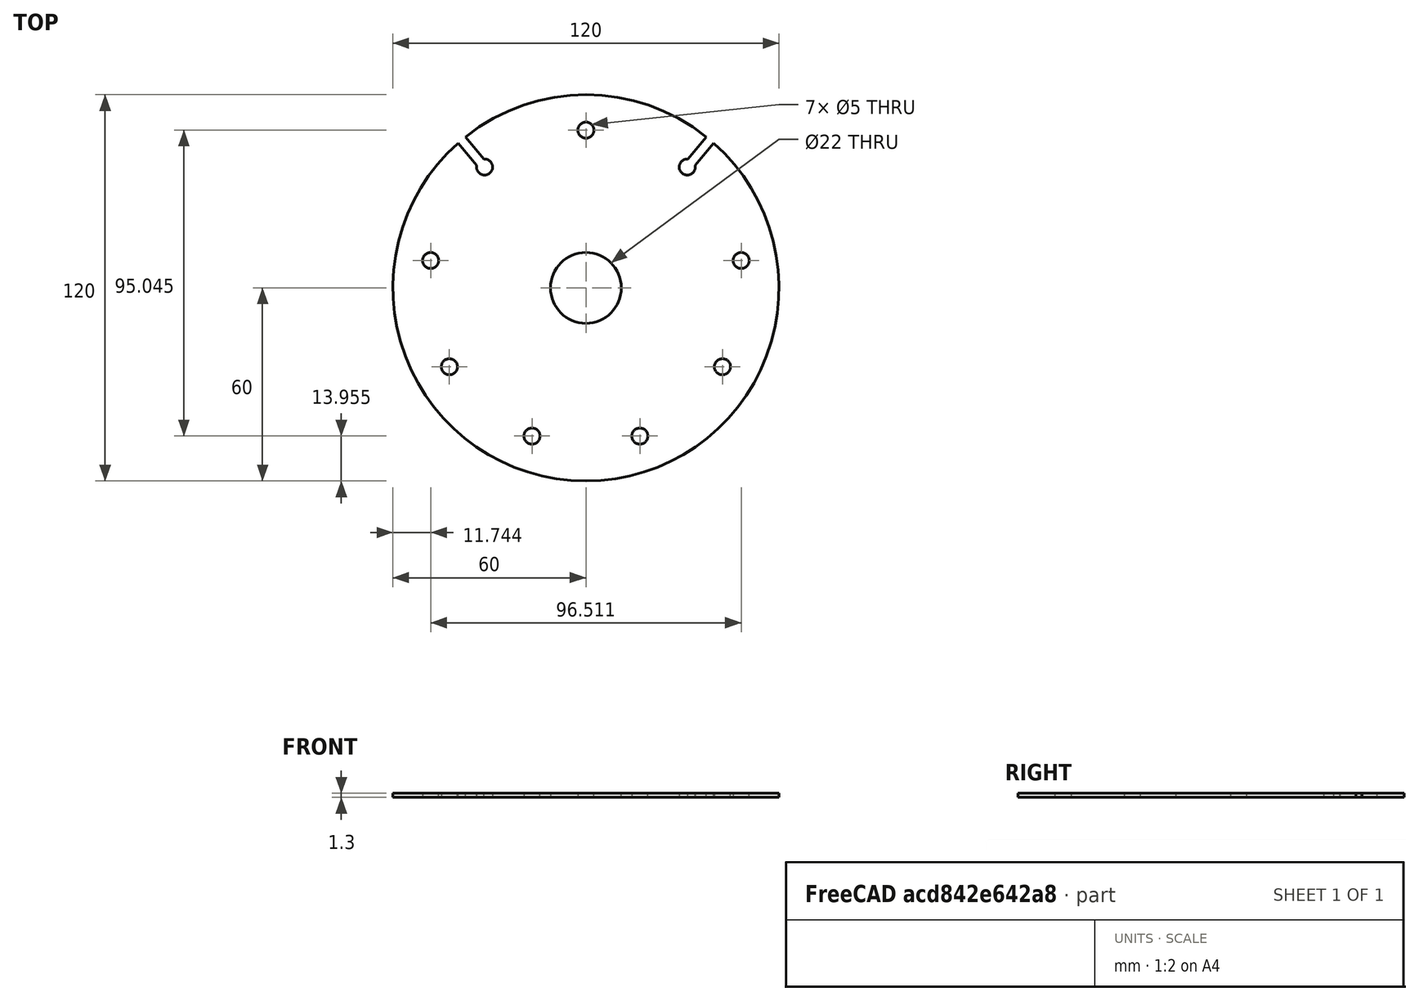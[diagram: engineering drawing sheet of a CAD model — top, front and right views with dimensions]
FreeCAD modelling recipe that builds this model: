
FCSTD DOCUMENT  (FreeCAD 0.19R24276 (Git))
Label: Disk_bolgarki_v2_d22_d120
License: All rights reserved
LicenseURL: http://en.wikipedia.org/wiki/All_rights_reserved
objects: Sketcher::SketchObject×1, PartDesign::Pad×1, PartDesign::Body×1
note: 4 computed .brp shape members not serialized (recipe doc carries the construction recipe); baked Part::Feature solids carry a one-line shape summary decoded from their .brp

FEATURE [Sketcher::SketchObject] Sketch
  FullyConstrained = false
  MapMode = 5
  Support = -> [XY_Plane]
  sketch-geometry (35):
    g0: Circle CenterX=0 CenterY=0 CenterZ=0 NormalX=0 NormalY=0 NormalZ=1 AngleXU=0 Radius=11
    g1: ArcOfCircle CenterX=0 CenterY=0 CenterZ=0 NormalX=0 NormalY=0 NormalZ=1 AngleXU=0 Radius=60 StartAngle=0.897667 EndAngle=2.24393
    g2: LineSegment StartX=0 StartY=49 StartZ=0 EndX=-31.4966 EndY=37.5362 EndZ=0
    g3: LineSegment StartX=-31.4966 StartY=37.5362 StartZ=0 EndX=-48.2556 EndY=8.50876 EndZ=0
    g4: LineSegment StartX=-48.2556 StartY=8.50876 StartZ=0 EndX=-42.4352 EndY=-24.5 EndZ=0
    g5: LineSegment StartX=-42.4352 StartY=-24.5 StartZ=0 EndX=-16.759 EndY=-46.0449 EndZ=0
    g6: LineSegment StartX=-16.759 StartY=-46.0449 StartZ=0 EndX=16.759 EndY=-46.0449 EndZ=0
    g7: LineSegment StartX=16.759 StartY=-46.0449 StartZ=0 EndX=42.4352 EndY=-24.5 EndZ=0
    g8: LineSegment StartX=42.4352 StartY=-24.5 StartZ=0 EndX=48.2556 EndY=8.50876 EndZ=0
    g9: LineSegment StartX=48.2556 StartY=8.50876 StartZ=0 EndX=31.4966 EndY=37.5362 EndZ=0
    g10: LineSegment StartX=31.4966 StartY=37.5362 StartZ=0 EndX=0 EndY=49 EndZ=0
    g11: Circle CenterX=0 CenterY=0 CenterZ=0 NormalX=0 NormalY=0 NormalZ=1 AngleXU=0 Radius=49
    g12: Circle CenterX=0 CenterY=49 CenterZ=0 NormalX=0 NormalY=0 NormalZ=1 AngleXU=0 Radius=2.5
    g13: ArcOfCircle CenterX=31.4966 CenterY=37.5362 CenterZ=0 NormalX=0 NormalY=0 NormalZ=1 AngleXU=0 Radius=2.5 StartAngle=1.51617 EndAngle=6.51235
    g14: Circle CenterX=48.2556 CenterY=8.50876 CenterZ=0 NormalX=0 NormalY=0 NormalZ=1 AngleXU=0 Radius=2.5
    g15: Circle CenterX=42.4352 CenterY=-24.5 CenterZ=0 NormalX=0 NormalY=0 NormalZ=1 AngleXU=0 Radius=2.5
    g16: Circle CenterX=16.759 CenterY=-46.0449 CenterZ=0 NormalX=0 NormalY=0 NormalZ=1 AngleXU=0 Radius=2.5
    g17: Circle CenterX=-16.759 CenterY=-46.0449 CenterZ=0 NormalX=0 NormalY=0 NormalZ=1 AngleXU=0 Radius=2.5
    g18: Circle CenterX=-42.4352 CenterY=-24.5 CenterZ=0 NormalX=0 NormalY=0 NormalZ=1 AngleXU=0 Radius=2.5
    g19: Circle CenterX=-48.2556 CenterY=8.50876 CenterZ=0 NormalX=0 NormalY=0 NormalZ=1 AngleXU=0 Radius=2.5
    g20: ArcOfCircle CenterX=-31.4966 CenterY=37.5362 CenterZ=0 NormalX=0 NormalY=0 NormalZ=1 AngleXU=0 Radius=2.5 StartAngle=2.91243 EndAngle=7.90861
    g21: LineSegment StartX=0 StartY=0 StartZ=0 EndX=31.4966 EndY=37.5362 EndZ=0
    g22: LineSegment StartX=32.6457 StartY=36.572 StartZ=0 EndX=39.7043 EndY=44.9841 EndZ=0
    g23: LineSegment StartX=30.3475 StartY=38.5004 StartZ=0 EndX=37.4061 EndY=46.9125 EndZ=0
    g24: LineSegment StartX=30.3475 StartY=38.5004 StartZ=0 EndX=32.6457 EndY=36.572 EndZ=0
    g25: LineSegment StartX=31.4966 StartY=37.5362 StartZ=0 EndX=38.5673 EndY=45.9627 EndZ=0
    g26: LineSegment StartX=33.9312 StartY=38.1041 StartZ=0 EndX=39.7043 EndY=44.9841 EndZ=0
    g27: LineSegment StartX=31.6331 StartY=40.0324 StartZ=0 EndX=37.4061 EndY=46.9125 EndZ=0
    g28: LineSegment StartX=-30.3475 StartY=38.5004 StartZ=0 EndX=-37.4061 EndY=46.9125 EndZ=0
    g29: LineSegment StartX=-32.6457 StartY=36.572 StartZ=0 EndX=-39.7043 EndY=44.9841 EndZ=0
    g30: LineSegment StartX=0 StartY=0 StartZ=0 EndX=-31.4966 EndY=37.5362 EndZ=0
    g31: LineSegment StartX=-32.6457 StartY=36.572 StartZ=0 EndX=-30.3475 EndY=38.5004 EndZ=0
    g32: ArcOfCircle CenterX=0 CenterY=0 CenterZ=0 NormalX=0 NormalY=0 NormalZ=1 AngleXU=0 Radius=60 StartAngle=2.29393 EndAngle=7.13085
    g33: LineSegment StartX=-33.9312 StartY=38.1041 StartZ=0 EndX=-39.7043 EndY=44.9841 EndZ=0
    g34: LineSegment StartX=-37.4061 StartY=46.9125 StartZ=0 EndX=-31.6331 EndY=40.0324 EndZ=0
  constraints (82):
    c: Coincident(g0,g-1)
    c: Coincident(g1,g0)
    c: Coincident(g2,g3)
    c: Coincident(g3,g4)
    c: Coincident(g4,g5)
    c: Coincident(g5,g6)
    c: Coincident(g6,g7)
    c: Coincident(g7,g8)
    c: Coincident(g8,g9)
    c: Coincident(g9,g10)
    c: Coincident(g10,g2)
    c: Equal(g2, g3-g10) x8
    c: PointOnObject(g2,g11)
    c: PointOnObject(g3,g11)
    c: PointOnObject(g4,g11)
    c: PointOnObject(g5,g11)
    c: PointOnObject(g6,g11)
    c: PointOnObject(g7,g11)
    c: PointOnObject(g8,g11)
    c: PointOnObject(g9,g11)
    c: PointOnObject(g10,g11)
    c: Coincident(g11,g0)
    c: PointOnObject(g10,g-2)
    c: Diameter(g11) = 98
    c: Diameter(g0) = 22
    c: Diameter(g1) = 120
    c: Coincident(g12,g2)
    c: Diameter(g12) = 5
    c: Coincident(g13,g9)
    c: Coincident(g14,g8)
    c: Coincident(g15,g7)
    c: Coincident(g16,g6)
    c: Coincident(g17,g5)
    c: Coincident(g18,g4)
    c: Coincident(g19,g3)
    c: Coincident(g20,g2)
    c: Equal(g20,g13)
    c: Equal(g13,g14)
    c: Equal(g14,g15)
    c: Equal(g15,g16)
    c: Equal(g16,g17)
    c: Equal(g17,g18)
    c: Equal(g18,g19)
    c: Equal(g19,g12)
    c: Coincident(g21,g0)
    c: Coincident(g21,g13)
    c: Parallel(g23,g21)
    c: Parallel(g22,g21)
    c: Coincident(g24,g23)
    c: Coincident(g24,g22)
    c: Perpendicular(g23,g24)
    c: Parallel(g25,g22)
    c: Symmetric(g22,g23,g25)
    c: Coincident(g25,g13)
    c: Coincident(g1,g23)
    c: Coincident(g32,g22)
    c: PointOnObject(g13,g22)
    c: PointOnObject(g13,g23)
    c: Coincident(g26,g13)
    c: Coincident(g27,g13)
    c: Coincident(g27,g1)
    c: Coincident(g26,g32)
    c: Coincident(g30,g0)
    c: Coincident(g30,g20)
    c: Parallel(g28,g30)
    c: Parallel(g29,g30)
    c: Coincident(g31,g29)
    c: Coincident(g31,g28)
    c: Perpendicular(g31,g28)
    c: Symmetric(g29,g28,g20)
    c: Distance(g29,g28) = 3
    c: Equal(g1,g32)
    c: Coincident(g1,g28)
    c: Coincident(g32,g29)
    c: Coincident(g1,g32)
    c: PointOnObject(g20,g29)
    c: PointOnObject(g20,g28)
    c: Distance(g1,g26) = 3
    c: Coincident(g33,g20)
    c: Coincident(g34,g1)
    c: Coincident(g34,g20)
    c: Coincident(g33,g32)
FEATURE [PartDesign::Pad] Pad
  Direction = (1,1,1)
  Length = 1.3
  Length2 = 100
  Profile = -> Sketch
  Type = 0
FEATURE [PartDesign::Body] Body
  Group = -> [Sketch,Pad]
  Origin = -> Origin
  Tip = -> Pad
